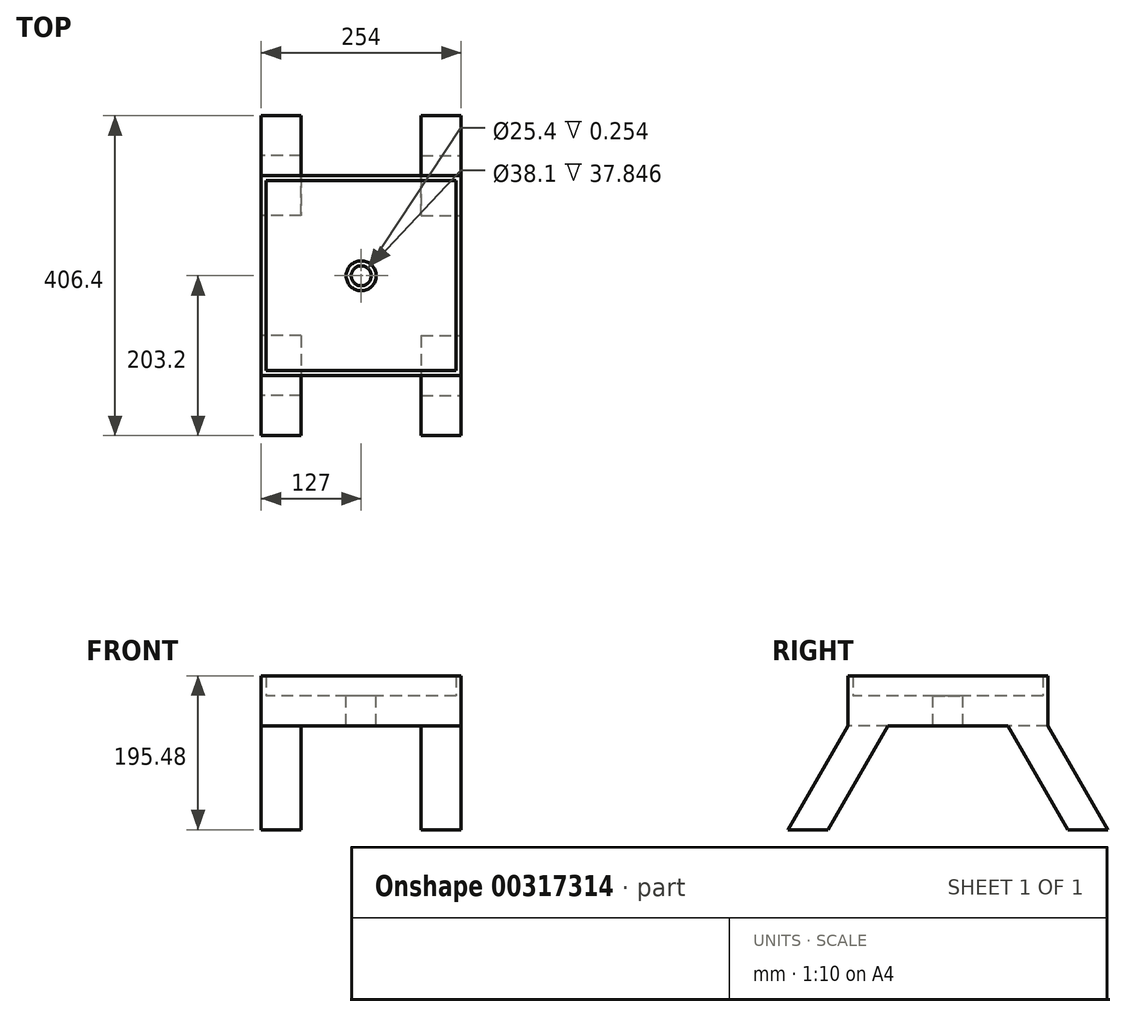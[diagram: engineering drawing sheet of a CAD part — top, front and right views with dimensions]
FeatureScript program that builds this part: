
annotation { "Feature Type Name" : "Feature", "Feature Type Description" : "" }
export const myFeature = defineFeature(function(context is Context, id is Id, definition is map)
    precondition{}
    {
        {
            var Q0;
            Q0=qCreatedBy(makeId("Top.planeOp"),FACE);
            var sketch = newSketch(context, id + "F0", { "sketchPlane" : qUnion([Q0])});
            skLineSegment(sketch, "E0.bottom", {"start": v(127, 127) * mm, "end": v(-127, 127) * mm});
            skLineSegment(sketch, "E0.top", {"start": v(127, -127) * mm, "end": v(-127, -127) * mm});
            skLineSegment(sketch, "E0.left", {"start": v(127, 127) * mm, "end": v(127, -127) * mm});
            skLineSegment(sketch, "E0.right", {"start": v(-127, 127) * mm, "end": v(-127, -127) * mm});
            skPoint(sketch, "E0.middle", {"position": v(0, 0) * mm});
            skCircle(sketch, "E1", {"center": v(0, 0) * mm, "radius": 12.7 * mm});
            skSolve(sketch);
        }
        {
            var Q0;
            Q0 = qSketchRegion(id + "F0", true);
            extrude(context, id + "F1", {"entities" : qUnion([Q0]), "oppositeDirection" : true, "depth" : 38.1 * mm});
        }
        {
            var Q0;
            Q0=makeQuery(id+"F1.opExtrude","CAP_FACE",FACE,{"disambiguationData":[OSD([sQuery(id+"F0.wireOp",EDGE,"E0.bottom"),sQuery(id+"F0.wireOp",EDGE,"E0.top"),sQuery(id+"F0.wireOp",EDGE,"E0.left"),sQuery(id+"F0.wireOp",EDGE,"E0.right"),sQuery(id+"F0.wireOp",EDGE,"E1")])],"isStart":true});
            var sketch = newSketch(context, id + "F2", { "sketchPlane" : qUnion([Q0])});
            skLineSegment(sketch, "E2.bottom", {"start": v(120.65, 120.65) * mm, "end": v(-120.65, 120.65) * mm});
            skLineSegment(sketch, "E2.top", {"start": v(120.65, -120.65) * mm, "end": v(-120.65, -120.65) * mm});
            skLineSegment(sketch, "E2.left", {"start": v(120.65, 120.65) * mm, "end": v(120.65, -120.65) * mm});
            skLineSegment(sketch, "E2.right", {"start": v(-120.65, 120.65) * mm, "end": v(-120.65, -120.65) * mm});
            skPoint(sketch, "E2.middle", {"position": v(0, 0) * mm});
            skLineSegment(sketch, "E3.bottom", {"start": v(127, 127) * mm, "end": v(-127, 127) * mm});
            skLineSegment(sketch, "E3.top", {"start": v(127, -127) * mm, "end": v(-127, -127) * mm});
            skLineSegment(sketch, "E3.left", {"start": v(127, 127) * mm, "end": v(127, -127) * mm});
            skLineSegment(sketch, "E3.right", {"start": v(-127, 127) * mm, "end": v(-127, -127) * mm});
            skSolve(sketch);
        }
        {
            var Q0;
            Q0 = qSketchRegion(id + "F2", true);
            extrude(context, id + "F3", {"entities" : qUnion([Q0]), "operationType" : NewBodyOperationType.ADD, "depth" : 25.4 * mm});
        }
        {
            var Q0;
            Q0=makeQuery(id+"F1.opExtrude","CAP_FACE",FACE,{"disambiguationData":[OSD([sQuery(id+"F0.wireOp",EDGE,"E0.bottom"),sQuery(id+"F0.wireOp",EDGE,"E0.top"),sQuery(id+"F0.wireOp",EDGE,"E0.left"),sQuery(id+"F0.wireOp",EDGE,"E0.right"),sQuery(id+"F0.wireOp",EDGE,"E1")])],"isStart":true});
            var sketch = newSketch(context, id + "F4", { "sketchPlane" : qUnion([Q0])});
            skCircle(sketch, "E4", {"center": v(0, 0) * mm, "radius": 19.05 * mm});
            skSolve(sketch);
        }
        {
            var Q0;
            Q0 = qSketchRegion(id + "F4", true);
            extrude(context, id + "F5", {"entities" : qUnion([Q0]), "operationType" : NewBodyOperationType.REMOVE, "oppositeDirection" : true, "depth" : 37.85 * mm});
        }
        {
            var Q0;
            Q0=makeQuery(id+"F3.boolean.opBoolean","MERGE",FACE,{"derivedFrom":[makeQuery(id+"F1.opExtrude","SWEPT_FACE",FACE,{"disambiguationData":[OSD([sQuery(id+"F0.wireOp",EDGE,"E0.right")])]}),makeQuery(id+"F3.opExtrude","SWEPT_FACE",FACE,{"disambiguationData":[OSD([sQuery(id+"F2.wireOp",EDGE,"E3.right")])]})]});
            var sketch = newSketch(context, id + "F6", { "sketchPlane" : qUnion([Q0])});
            skLineSegment(sketch, "E5", {"start": v(127, -38.1) * mm, "end": v(76.2, -38.1) * mm});
            skLineSegment(sketch, "E6", {"start": v(76.2, -38.1) * mm, "end": v(152.4, -170.08) * mm});
            skLineSegment(sketch, "E7", {"start": v(127, -38.1) * mm, "end": v(203.2, -170.08) * mm});
            skLineSegment(sketch, "E8", {"start": v(152.4, -170.08) * mm, "end": v(203.2, -170.08) * mm});
            skLineSegment(sketch, "E9", {"start": v(0, 25.4) * mm, "end": v(0, -38.1) * mm});
            skLineSegment(sketch, "E10.MirrorCS", {"start": v(-127, -38.1) * mm, "end": v(-76.2, -38.1) * mm});
            skLineSegment(sketch, "E11.MirrorCS", {"start": v(-76.2, -38.1) * mm, "end": v(-152.4, -170.08) * mm});
            skLineSegment(sketch, "E12.MirrorCS", {"start": v(-152.4, -170.08) * mm, "end": v(-203.2, -170.08) * mm});
            skLineSegment(sketch, "E13.MirrorCS", {"start": v(-127, -38.1) * mm, "end": v(-203.2, -170.08) * mm});
            skSolve(sketch);
        }
        {
            var Q0;
            Q0 = qSketchRegion(id + "F6", true);
            extrude(context, id + "F7", {"entities" : qUnion([Q0]), "operationType" : NewBodyOperationType.ADD, "oppositeDirection" : true, "depth" : 50.8 * mm});
        }
        {
            var Q0;
            Q0=makeQuery(id+"F3.boolean.opBoolean","MERGE",FACE,{"derivedFrom":[makeQuery(id+"F1.opExtrude","SWEPT_FACE",FACE,{"disambiguationData":[OSD([sQuery(id+"F0.wireOp",EDGE,"E0.left")])]}),makeQuery(id+"F3.opExtrude","SWEPT_FACE",FACE,{"disambiguationData":[OSD([sQuery(id+"F2.wireOp",EDGE,"E3.left")])]})]});
            var sketch = newSketch(context, id + "F8", { "sketchPlane" : qUnion([Q0])});
            skLineSegment(sketch, "E14", {"start": v(-127, -38.1) * mm, "end": v(-76.2, -38.1) * mm});
            skLineSegment(sketch, "E15", {"start": v(-76.2, -38.1) * mm, "end": v(-152.4, -170.08) * mm});
            skLineSegment(sketch, "E16", {"start": v(-152.4, -170.08) * mm, "end": v(-203.2, -170.08) * mm});
            skLineSegment(sketch, "E17", {"start": v(-203.2, -170.08) * mm, "end": v(-127, -38.1) * mm});
            skLineSegment(sketch, "E18", {"start": v(0, 25.4) * mm, "end": v(0, -38.1) * mm});
            skLineSegment(sketch, "E19.MirrorCS", {"start": v(127, -38.1) * mm, "end": v(76.2, -38.1) * mm});
            skLineSegment(sketch, "E20.MirrorCS", {"start": v(76.2, -38.1) * mm, "end": v(152.4, -170.08) * mm});
            skLineSegment(sketch, "E21.MirrorCS", {"start": v(203.2, -170.08) * mm, "end": v(127, -38.1) * mm});
            skLineSegment(sketch, "E22.MirrorCS", {"start": v(152.4, -170.08) * mm, "end": v(203.2, -170.08) * mm});
            skSolve(sketch);
        }
        {
            var Q0;
            Q0 = qSketchRegion(id + "F8", true);
            extrude(context, id + "F9", {"entities" : qUnion([Q0]), "operationType" : NewBodyOperationType.ADD, "oppositeDirection" : true, "depth" : 50.8 * mm});
        }
    });
